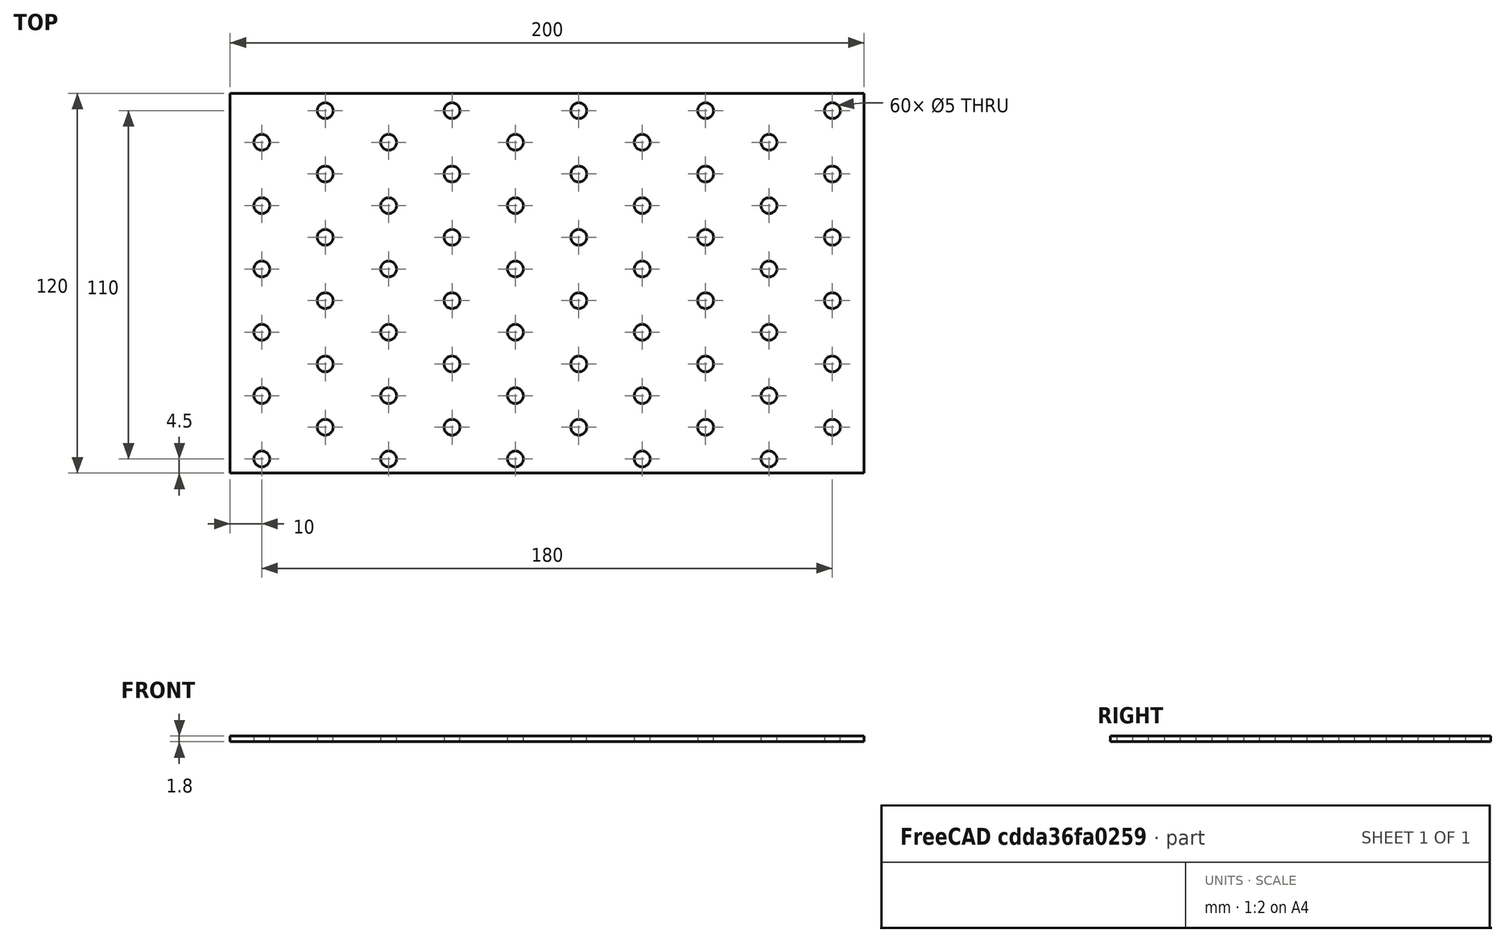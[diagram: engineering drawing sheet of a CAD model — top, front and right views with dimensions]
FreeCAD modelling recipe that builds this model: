
FCSTD DOCUMENT  (FreeCAD 0.19R24276 (Git))
Label: Bar_120x200__1_8mm
License: All rights reserved
LicenseURL: http://en.wikipedia.org/wiki/All_rights_reserved
objects: Sketcher::SketchObject×1, PartDesign::Pad×1, PartDesign::Body×1
note: 4 computed .brp shape members not serialized (recipe doc carries the construction recipe); baked Part::Feature solids carry a one-line shape summary decoded from their .brp

FEATURE [Sketcher::SketchObject] Sketch
  FullyConstrained = false
  MapMode = 5
  Support = -> [XY_Plane]
  sketch-geometry (64):
    g0: Circle CenterX=0 CenterY=0 CenterZ=0 NormalX=0 NormalY=0 NormalZ=1 AngleXU=0 Radius=2.5
    g1: Circle CenterX=0 CenterY=20 CenterZ=0 NormalX=0 NormalY=0 NormalZ=1 AngleXU=0 Radius=2.5
    g2: Circle CenterX=0 CenterY=40 CenterZ=0 NormalX=0 NormalY=0 NormalZ=1 AngleXU=0 Radius=2.5
    g3: Circle CenterX=0 CenterY=60 CenterZ=0 NormalX=0 NormalY=0 NormalZ=1 AngleXU=0 Radius=2.5
    g4: Circle CenterX=20 CenterY=10 CenterZ=0 NormalX=0 NormalY=0 NormalZ=1 AngleXU=0 Radius=2.5
    g5: Circle CenterX=20 CenterY=30 CenterZ=0 NormalX=0 NormalY=0 NormalZ=1 AngleXU=0 Radius=2.5
    g6: Circle CenterX=20 CenterY=50 CenterZ=0 NormalX=0 NormalY=0 NormalZ=1 AngleXU=0 Radius=2.5
    g7: Circle CenterX=20 CenterY=70 CenterZ=0 NormalX=0 NormalY=0 NormalZ=1 AngleXU=0 Radius=2.5
    g8: Circle CenterX=40 CenterY=0 CenterZ=0 NormalX=0 NormalY=0 NormalZ=1 AngleXU=0 Radius=2.5
    g9: Circle CenterX=40 CenterY=20 CenterZ=0 NormalX=0 NormalY=0 NormalZ=1 AngleXU=0 Radius=2.5
    g10: Circle CenterX=40 CenterY=40 CenterZ=0 NormalX=0 NormalY=0 NormalZ=1 AngleXU=0 Radius=2.5
    g11: Circle CenterX=40 CenterY=60 CenterZ=0 NormalX=0 NormalY=0 NormalZ=1 AngleXU=0 Radius=2.5
    g12: Circle CenterX=60 CenterY=10 CenterZ=0 NormalX=0 NormalY=0 NormalZ=1 AngleXU=0 Radius=2.5
    g13: Circle CenterX=60 CenterY=30 CenterZ=0 NormalX=0 NormalY=0 NormalZ=1 AngleXU=0 Radius=2.5
    g14: Circle CenterX=60 CenterY=50 CenterZ=0 NormalX=0 NormalY=0 NormalZ=1 AngleXU=0 Radius=2.5
    g15: Circle CenterX=60 CenterY=70 CenterZ=0 NormalX=0 NormalY=0 NormalZ=1 AngleXU=0 Radius=2.5
    g16: Circle CenterX=80 CenterY=0 CenterZ=0 NormalX=0 NormalY=0 NormalZ=1 AngleXU=0 Radius=2.5
    g17: Circle CenterX=80 CenterY=20 CenterZ=0 NormalX=0 NormalY=0 NormalZ=1 AngleXU=0 Radius=2.5
    g18: Circle CenterX=80 CenterY=40 CenterZ=0 NormalX=0 NormalY=0 NormalZ=1 AngleXU=0 Radius=2.5
    g19: Circle CenterX=80 CenterY=60 CenterZ=0 NormalX=0 NormalY=0 NormalZ=1 AngleXU=0 Radius=2.5
    g20: Circle CenterX=100 CenterY=10 CenterZ=0 NormalX=0 NormalY=0 NormalZ=1 AngleXU=0 Radius=2.5
    g21: Circle CenterX=100 CenterY=30 CenterZ=0 NormalX=0 NormalY=0 NormalZ=1 AngleXU=0 Radius=2.5
    g22: Circle CenterX=100 CenterY=50 CenterZ=0 NormalX=0 NormalY=0 NormalZ=1 AngleXU=0 Radius=2.5
    g23: Circle CenterX=100 CenterY=70 CenterZ=0 NormalX=0 NormalY=0 NormalZ=1 AngleXU=0 Radius=2.5
    g24: Circle CenterX=120 CenterY=0 CenterZ=0 NormalX=0 NormalY=0 NormalZ=1 AngleXU=0 Radius=2.5
    g25: Circle CenterX=120 CenterY=20 CenterZ=0 NormalX=0 NormalY=0 NormalZ=1 AngleXU=0 Radius=2.5
    g26: Circle CenterX=120 CenterY=40 CenterZ=0 NormalX=0 NormalY=0 NormalZ=1 AngleXU=0 Radius=2.5
    g27: Circle CenterX=120 CenterY=60 CenterZ=0 NormalX=0 NormalY=0 NormalZ=1 AngleXU=0 Radius=2.5
    g28: Circle CenterX=140 CenterY=10 CenterZ=0 NormalX=0 NormalY=0 NormalZ=1 AngleXU=0 Radius=2.5
    g29: Circle CenterX=140 CenterY=30 CenterZ=0 NormalX=0 NormalY=0 NormalZ=1 AngleXU=0 Radius=2.5
    g30: Circle CenterX=140 CenterY=50 CenterZ=0 NormalX=0 NormalY=0 NormalZ=1 AngleXU=0 Radius=2.5
    g31: Circle CenterX=140 CenterY=70 CenterZ=0 NormalX=0 NormalY=0 NormalZ=1 AngleXU=0 Radius=2.5
    g32: LineSegment StartX=-10 StartY=115.5 StartZ=0 EndX=190 EndY=115.5 EndZ=0
    g33: LineSegment StartX=190 StartY=115.5 StartZ=0 EndX=190 EndY=-4.5 EndZ=0
    g34: LineSegment StartX=190 StartY=-4.5 StartZ=0 EndX=-10 EndY=-4.5 EndZ=0
    g35: LineSegment StartX=-10 StartY=-4.5 StartZ=0 EndX=-10 EndY=115.5 EndZ=0
    g36: Circle CenterX=160 CenterY=0 CenterZ=0 NormalX=0 NormalY=0 NormalZ=1 AngleXU=0 Radius=2.5
    g37: Circle CenterX=160 CenterY=20 CenterZ=0 NormalX=0 NormalY=0 NormalZ=1 AngleXU=0 Radius=2.5
    g38: Circle CenterX=160 CenterY=40 CenterZ=0 NormalX=0 NormalY=0 NormalZ=1 AngleXU=0 Radius=2.5
    g39: Circle CenterX=160 CenterY=60 CenterZ=0 NormalX=0 NormalY=0 NormalZ=1 AngleXU=0 Radius=2.5
    g40: Circle CenterX=180 CenterY=10 CenterZ=0 NormalX=0 NormalY=0 NormalZ=1 AngleXU=0 Radius=2.5
    g41: Circle CenterX=180 CenterY=30 CenterZ=0 NormalX=0 NormalY=0 NormalZ=1 AngleXU=0 Radius=2.5
    g42: Circle CenterX=180 CenterY=50 CenterZ=0 NormalX=0 NormalY=0 NormalZ=1 AngleXU=0 Radius=2.5
    g43: Circle CenterX=180 CenterY=70 CenterZ=0 NormalX=0 NormalY=0 NormalZ=1 AngleXU=0 Radius=2.5
    g44: Circle CenterX=0 CenterY=80 CenterZ=0 NormalX=0 NormalY=0 NormalZ=1 AngleXU=0 Radius=2.5
    g45: Circle CenterX=20 CenterY=90 CenterZ=0 NormalX=0 NormalY=0 NormalZ=1 AngleXU=0 Radius=2.5
    g46: Circle CenterX=40 CenterY=80 CenterZ=0 NormalX=0 NormalY=0 NormalZ=1 AngleXU=0 Radius=2.5
    g47: Circle CenterX=60 CenterY=90 CenterZ=0 NormalX=0 NormalY=0 NormalZ=1 AngleXU=0 Radius=2.5
    g48: Circle CenterX=80 CenterY=80 CenterZ=0 NormalX=0 NormalY=0 NormalZ=1 AngleXU=0 Radius=2.5
    g49: Circle CenterX=100 CenterY=90 CenterZ=0 NormalX=0 NormalY=0 NormalZ=1 AngleXU=0 Radius=2.5
    g50: Circle CenterX=120 CenterY=80 CenterZ=0 NormalX=0 NormalY=0 NormalZ=1 AngleXU=0 Radius=2.5
    g51: Circle CenterX=140 CenterY=90 CenterZ=0 NormalX=0 NormalY=0 NormalZ=1 AngleXU=0 Radius=2.5
    g52: Circle CenterX=160 CenterY=80 CenterZ=0 NormalX=0 NormalY=0 NormalZ=1 AngleXU=0 Radius=2.5
    g53: Circle CenterX=180 CenterY=90 CenterZ=0 NormalX=0 NormalY=0 NormalZ=1 AngleXU=0 Radius=2.5
    g54: Circle CenterX=0 CenterY=100 CenterZ=0 NormalX=0 NormalY=0 NormalZ=1 AngleXU=0 Radius=2.5
    g55: Circle CenterX=40 CenterY=100 CenterZ=0 NormalX=0 NormalY=0 NormalZ=1 AngleXU=0 Radius=2.5
    g56: Circle CenterX=80 CenterY=100 CenterZ=0 NormalX=0 NormalY=0 NormalZ=1 AngleXU=0 Radius=2.5
    g57: Circle CenterX=120 CenterY=100 CenterZ=0 NormalX=0 NormalY=0 NormalZ=1 AngleXU=0 Radius=2.5
    g58: Circle CenterX=160 CenterY=100 CenterZ=0 NormalX=0 NormalY=0 NormalZ=1 AngleXU=0 Radius=2.5
    g59: Circle CenterX=20 CenterY=110 CenterZ=0 NormalX=0 NormalY=0 NormalZ=1 AngleXU=0 Radius=2.5
    g60: Circle CenterX=60 CenterY=110 CenterZ=0 NormalX=0 NormalY=0 NormalZ=1 AngleXU=0 Radius=2.5
    g61: Circle CenterX=100 CenterY=110 CenterZ=0 NormalX=0 NormalY=0 NormalZ=1 AngleXU=0 Radius=2.5
    g62: Circle CenterX=140 CenterY=110 CenterZ=0 NormalX=0 NormalY=0 NormalZ=1 AngleXU=0 Radius=2.5
    g63: Circle CenterX=180 CenterY=110 CenterZ=0 NormalX=0 NormalY=0 NormalZ=1 AngleXU=0 Radius=2.5
  constraints (187):
    c: Coincident(g0,g-1)
    c: PointOnObject(g1,g-2)
    c: PointOnObject(g2,g-2)
    c: PointOnObject(g3,g-2)
    c: Diameter(g0) = 5
    c: Equal(g0,g1)
    c: Equal(g0,g2)
    c: Equal(g0,g3)
    c: DistanceY(g0,g1) = 20
    c: DistanceY(g1,g2) = 20
    c: DistanceY(g2,g3) = 20
    c: Equal(g0,g4) = 5
    c: Equal(g4,g5)
    c: Equal(g4,g6)
    c: Equal(g4,g7)
    c: DistanceY(g4,g5) = 20
    c: DistanceY(g5,g6) = 20
    c: DistanceY(g6,g7) = 20
    c: DistanceY(g0,g4) = 10
    c: DistanceX(g0,g4) = 20
    c: DistanceX(g5,g4) = 0
    c: DistanceX(g6,g5) = 0
    c: DistanceX(g7,g6) = 0
    c: Equal(g0,g8) = 5
    c: Equal(g8,g9)
    c: Equal(g8,g10)
    c: Equal(g8,g11)
    c: DistanceY(g8,g9) = 20
    c: DistanceY(g9,g10) = 20
    c: DistanceY(g10,g11) = 20
    c: Equal(g8,g12) = 5
    c: Equal(g12,g13)
    c: Equal(g12,g14)
    c: Equal(g12,g15)
    c: DistanceY(g12,g13) = 20
    c: DistanceY(g13,g14) = 20
    c: DistanceY(g14,g15) = 20
    c: DistanceY(g8,g12) = 10
    c: DistanceX(g8,g12) = 20
    c: DistanceX(g13,g12) = 0
    c: DistanceX(g14,g13) = 0
    c: DistanceX(g15,g14) = 0
    c: DistanceY(g8,g0) = 0
    c: DistanceX(g9,g8) = 0
    c: DistanceX(g9,g10) = 0
    c: DistanceX(g11,g10) = 0
    c: DistanceX(g4,g8) = 20
    c: Equal(g0,g16) = 5
    c: Equal(g16,g17)
    c: Equal(g16,g18)
    c: Equal(g16,g19)
    c: DistanceY(g16,g17) = 20
    c: DistanceY(g17,g18) = 20
    c: DistanceY(g18,g19) = 20
    c: Equal(g16,g20) = 5
    c: Equal(g20,g21)
    c: Equal(g20,g22)
    c: Equal(g20,g23)
    c: DistanceY(g20,g21) = 20
    c: DistanceY(g21,g22) = 20
    c: DistanceY(g22,g23) = 20
    c: DistanceY(g16,g20) = 10
    c: DistanceX(g16,g20) = 20
    c: DistanceX(g21,g20) = 0
    c: DistanceX(g22,g21) = 0
    c: DistanceX(g23,g22) = 0
    c: Equal(g16,g24) = 5
    c: Equal(g24,g25)
    c: Equal(g24,g26)
    c: Equal(g24,g27)
    c: DistanceY(g24,g25) = 20
    c: DistanceY(g25,g26) = 20
    c: DistanceY(g26,g27) = 20
    c: Equal(g24,g28) = 5
    c: Equal(g28,g29)
    c: Equal(g28,g30)
    c: Equal(g28,g31)
    c: DistanceY(g28,g29) = 20
    c: DistanceY(g29,g30) = 20
    c: DistanceY(g30,g31) = 20
    c: DistanceY(g24,g28) = 10
    c: DistanceX(g24,g28) = 20
    c: DistanceX(g29,g28) = 0
    c: DistanceX(g30,g29) = 0
    c: DistanceX(g31,g30) = 0
    c: DistanceY(g24,g16) = 0
    c: DistanceX(g25,g24) = 0
    c: DistanceX(g25,g26) = 0
    c: DistanceX(g27,g26) = 0
    c: DistanceX(g20,g24) = 20
    c: DistanceX(g16,g17) = 0
    c: DistanceX(g17,g18) = 0
    c: DistanceX(g18,g19) = 0
    c: DistanceX(g12,g16) = 20
    c: DistanceY(g8,g16) = 0
    c: Coincident(g32,g33)
    c: Coincident(g33,g34)
    c: Coincident(g34,g35)
    c: Horizontal(g32)
    c: Horizontal(g34)
    c: Vertical(g33)
    c: Vertical(g35)
    c: DistanceY(g33,g33) = 120
    c: DistanceY(g34,g0) = 4.5
    c: DistanceX(g34,g0) = 10
    c: Equal(g36,g37)
    c: Equal(g36,g38)
    c: Equal(g36,g39)
    c: DistanceY(g36,g37) = 20
    c: DistanceY(g37,g38) = 20
    c: DistanceY(g38,g39) = 20
    c: Equal(g36,g40) = 5
    c: Equal(g40,g41)
    c: Equal(g40,g42)
    c: Equal(g40,g43)
    c: DistanceY(g40,g41) = 20
    c: DistanceY(g41,g42) = 20
    c: DistanceY(g42,g43) = 20
    c: DistanceY(g36,g40) = 10
    c: DistanceX(g36,g40) = 20
    c: DistanceX(g41,g40) = 0
    c: DistanceX(g42,g41) = 0
    c: DistanceX(g43,g42) = 0
    c: DistanceX(g37,g36) = 0
    c: DistanceX(g37,g38) = 0
    c: DistanceX(g39,g38) = 0
    c: DistanceY(g36,g24) = 0
    c: DistanceX(g28,g36) = 20
    c: Equal(g0,g44) = 5
    c: Equal(g44,g45) = 5
    c: DistanceY(g44,g45) = 10
    c: DistanceX(g44,g45) = 20
    c: Equal(g44,g46) = 5
    c: Equal(g46,g47) = 5
    c: DistanceY(g46,g47) = 10
    c: DistanceX(g46,g47) = 20
    c: DistanceY(g46,g44) = 0
    c: DistanceX(g45,g46) = 20
    c: Equal(g44,g48) = 5
    c: Equal(g48,g49) = 5
    c: DistanceY(g48,g49) = 10
    c: DistanceX(g48,g49) = 20
    c: Equal(g48,g50) = 5
    c: Equal(g50,g51) = 5
    c: DistanceY(g50,g51) = 10
    c: DistanceX(g50,g51) = 20
    c: DistanceY(g50,g48) = 0
    c: DistanceX(g49,g50) = 20
    c: DistanceX(g47,g48) = 20
    c: DistanceY(g46,g48) = 0
    c: Equal(g52,g53) = 5
    c: DistanceY(g52,g53) = 10
    c: DistanceX(g52,g53) = 20
    c: DistanceY(g52,g50) = 0
    c: DistanceX(g51,g52) = 20
    c: DistanceX(g53,g43) = 0
    c: DistanceY(g43,g52) = 10
    c: DistanceX(g34,g34) = 200
    c: PointOnObject(g35,g32)
    c: Equal(g54,g59) = 5
    c: DistanceY(g54,g59) = 10
    c: DistanceX(g54,g59) = 20
    c: Equal(g54,g55) = 5
    c: Equal(g55,g60) = 5
    c: DistanceY(g55,g60) = 10
    c: DistanceX(g55,g60) = 20
    c: DistanceY(g55,g54) = 0
    c: DistanceX(g59,g55) = 20
    c: Equal(g54,g56) = 5
    c: Equal(g56,g61) = 5
    c: DistanceY(g56,g61) = 10
    c: DistanceX(g56,g61) = 20
    c: Equal(g56,g57) = 5
    c: Equal(g57,g62) = 5
    c: DistanceY(g57,g62) = 10
    c: DistanceX(g57,g62) = 20
    c: DistanceY(g57,g56) = 0
    c: DistanceX(g61,g57) = 20
    c: DistanceX(g60,g56) = 20
    c: DistanceY(g55,g56) = 0
    c: Equal(g58,g63) = 5
    c: DistanceY(g58,g63) = 10
    c: DistanceX(g58,g63) = 20
    c: DistanceY(g58,g57) = 0
    c: DistanceX(g62,g58) = 20
    c: DistanceX(g44,g54) = 0
    c: DistanceY(g45,g54) = 10
FEATURE [PartDesign::Pad] Pad
  Direction = (1,1,1)
  Length = 1.8
  Length2 = 100
  Profile = -> Sketch
  Type = 0
FEATURE [PartDesign::Body] Body
  Group = -> [Sketch,Pad]
  Origin = -> Origin
  Tip = -> Pad
